# Revit family: Talos RDR-C03
name_source: partatom
category: Türen
revit_build: Autodesk Revit 2016 (Build: 20150220_1215(x64)
units: mm (PartAtom-declared; Revit-internal decimal feet)

## family parameters
Beim Laden mit Abzugskörper schneiden = Nein
Gemeinsam genutzt = Nein
Immer vertikal = Ja
OmniClass-Nummer = 23.30.10.00
OmniClass-Titel = Doors
Raumberechnungspunkt = Nein

## types (9) — shared parameters
Analytische Konstruktion = <Keine Auswahl>
BIMobject category = Revolving
CoverMaterial = Glas
Date of publishing = 1/16/2017
Design country = Germany
Edition number = 1
ElementWeight = 0.00 kg
FrameMaterial = 1.4401 - A4
Funktion = Außen
HandlePosition = 35 mm  [stored 0.114829 ft]
HasCover = Ja
HasFoldableDoors = Ja
HasGrabHandles = Ja
Hersteller = Kaba GmbH
Konstruktionstyp = Revolving Door
Manufacturer = Kaba GmbH
Manufacturer country = Germany
Manufacturer name = DORMA
Material main = Glass
Material secondary = Metal
Modell = Talos RDR-E01
MotorDriveType = -
Nominal height = 2300
OperatingWeight = 0.00 kg
Product Guid = dcba0ff2-2df2-4dff-90c3-13034e0ede75
Product SKU = Talos_RDR-C03
Product data url = https://bimobject.com
Product family = Entrance
Product group = Special Doors
ProfileWidth = 40 mm  [stored 0.131234 ft]
QR code = http://bimobject.com
RubberMaterial = Zellkautschuk - EPDM
SectionWidth = 4300 mm
ShutOffDevice = Nein
ShutOffDeviceInside = Nein
Technical description = http://www.kaba.com
Type = Talos RDR-C03
URL = http://www.kaba.com
Weight = 0.00 kg
zero-valued in all types: Nominal width, Weight Net (Kg)

## per-type parameters (varying)
- RDR-C03 2000: AccessLengthOrRadius=1030 mm; BaseType=60 mm - 169 mm; ClearHeight=2100 mm; ConsoleS1=1129 mm  [stored 3.70407 ft]; ConsoleS2=1129 mm  [stored 3.70407 ft]; ConsoleType=console : Type 4; CoverWidth=200 mm  [stored 0.656168 ft]; Diameter=1060 mm; DiameterCoverFront=1140 mm  [stored 3.74016 ft]; DiameterGlassInside=1040 mm  [stored 3.41207 ft]; DiameterGlassOutside=1050 mm  [stored 3.44488 ft]; DiameterNightLock=1090 mm  [stored 3.57612 ft]; DiameterNightLockCover=1120 mm; DiameterNightLockFrame=1081 mm  [stored 3.54659 ft]; DiameterNightLockGlassInside=1101 mm; DiameterNightLockGlassOutside=1109 mm  [stored 3.63845 ft]; Dicke=40 mm  [stored 0.131234 ft]; DoorThickness=40 mm  [stored 0.131234 ft]; DoorThicknessLeft=-20 mm  [stored -0.0656168 ft]; DoorThicknessRight=20 mm  [stored 0.0656168 ft]; DoorWidth=930 mm  [stored 3.05118 ft]; HandleMaterial=1.4401 - A4; HasConsoleS1=Ja; HasConsoleS2=Ja; HasGrabHandles 120=Nein; HasGrabHandles 180=Ja; HasIntegralShutOffDevice=Ja; HasLock=Ja; HasLockInside=Ja; HasMotionSensor=Ja; HasShellTopFrame=Nein; Height=2300 mm; MotionSensorInside=1122 mm  [stored 3.6811 ft]; MotionSensorOutside=1122 mm  [stored 3.6811 ft]; OuterDiameter=2100 mm; ProfileCenter=0 mm  [stored 0 ft]; RotationInterval 120=Nein; RotationInterval 180=Ja; StandardUsed=Talos RDR-C01-32; Width=2100 mm
- RDR-C03 2200: AccessLengthOrRadius=1130 mm; BaseType=60 mm - 69 mm; ClearHeight=2300 mm; ConsoleS1=1181 mm; ConsoleS2=1229 mm; ConsoleType=console : Type 5; CoverWidth=100 mm  [stored 0.328084 ft]; Diameter=1160 mm; DiameterCoverFront=1240 mm; DiameterGlassInside=1140 mm  [stored 3.74016 ft]; DiameterGlassOutside=1150 mm; DiameterNightLock=1190 mm  [stored 3.9042 ft]; DiameterNightLockCover=1220 mm  [stored 4.00262 ft]; DiameterNightLockFrame=1181 mm; DiameterNightLockGlassInside=1201 mm; DiameterNightLockGlassOutside=1209 mm  [stored 3.96654 ft]; Dicke=25 mm  [stored 0.082021 ft]; DoorThickness=25 mm  [stored 0.082021 ft]; DoorThicknessLeft=-12.5 mm; DoorThicknessRight=12.5 mm; DoorWidth=1030 mm; HandleMaterial=1.4401 - A4; HasConsoleS1=Ja; HasConsoleS2=Ja; HasGrabHandles 120=Ja; HasGrabHandles 180=Nein; HasIntegralShutOffDevice=Nein; HasLock=Ja; HasLockInside=Nein; HasMotionSensor=Ja; HasShellTopFrame=Nein; Height=2400 mm; MotionSensorInside=1160 mm; MotionSensorOutside=1222 mm; OuterDiameter=2300 mm; ProfileCenter=7.5 mm; RotationInterval 120=Ja; RotationInterval 180=Nein; StandardUsed=Talos RDR-C01-33; Width=2300 mm
- RDR-C03 2400: AccessLengthOrRadius=1230 mm  [stored 4.03543 ft]; BaseType=60 mm - 69 mm; ClearHeight=2300 mm; ConsoleS1=1281 mm; ConsoleS2=1281 mm; ConsoleType=console : Type 4; CoverWidth=300 mm; Diameter=1260 mm  [stored 4.13386 ft]; DiameterCoverFront=1340 mm; DiameterGlassInside=1240 mm; DiameterGlassOutside=1250 mm  [stored 4.10105 ft]; DiameterNightLock=1290 mm; DiameterNightLockCover=1320 mm; DiameterNightLockFrame=1281 mm; DiameterNightLockGlassInside=1301 mm; DiameterNightLockGlassOutside=1309 mm; Dicke=25 mm  [stored 0.082021 ft]; DoorThickness=25 mm  [stored 0.082021 ft]; DoorThicknessLeft=-12.5 mm; DoorThicknessRight=12.5 mm; DoorWidth=1130 mm; HandleMaterial=PA6.6 Gf30(schwarz); HasConsoleS1=Ja; HasConsoleS2=Ja; HasGrabHandles 120=Nein; HasGrabHandles 180=Ja; HasIntegralShutOffDevice=Nein; HasLock=Nein; HasLockInside=Nein; HasMotionSensor=Nein; HasShellTopFrame=Ja; Height=2600 mm; MotionSensorInside=1260 mm  [stored 4.13386 ft]; MotionSensorOutside=1260 mm  [stored 4.13386 ft]; OuterDiameter=2500 mm; ProfileCenter=7.5 mm; RotationInterval 120=Nein; RotationInterval 180=Ja; StandardUsed=Talos RDR-C01-34; Width=2500 mm
- RDR-C03 2600: AccessLengthOrRadius=1330 mm; BaseType=60 mm - 99 mm; ClearHeight=2100 mm; ConsoleS1=1381 mm; ConsoleS2=1381 mm; ConsoleType=console : Type 5; CoverWidth=200 mm  [stored 0.656168 ft]; Diameter=1360 mm; DiameterCoverFront=1440 mm; DiameterGlassInside=1340 mm; DiameterGlassOutside=1350 mm; DiameterNightLock=1390 mm; DiameterNightLockCover=1420 mm; DiameterNightLockFrame=1381 mm; DiameterNightLockGlassInside=1401 mm; DiameterNightLockGlassOutside=1409 mm; Dicke=40 mm  [stored 0.131234 ft]; DoorThickness=40 mm  [stored 0.131234 ft]; DoorThicknessLeft=-20 mm  [stored -0.0656168 ft]; DoorThicknessRight=20 mm  [stored 0.0656168 ft]; DoorWidth=1230 mm  [stored 4.03543 ft]; HandleMaterial=1.4401 - A4; HasConsoleS1=Ja; HasConsoleS2=Ja; HasGrabHandles 120=Ja; HasGrabHandles 180=Nein; HasIntegralShutOffDevice=Nein; HasLock=Nein; HasLockInside=Nein; HasMotionSensor=Nein; HasShellTopFrame=Nein; Height=2300 mm; MotionSensorInside=1360 mm; MotionSensorOutside=1360 mm; OuterDiameter=2700 mm; ProfileCenter=0 mm  [stored 0 ft]; RotationInterval 120=Ja; RotationInterval 180=Nein; StandardUsed=Talos RDR-C01-35; Width=2700 mm
- RDR-C03 2800: AccessLengthOrRadius=1430 mm; BaseType=60 mm - 190 mm; ClearHeight=2200 mm; ConsoleS1=1481 mm; ConsoleS2=1481 mm; ConsoleType=console : Type 4; CoverWidth=300 mm; Diameter=1460 mm; DiameterCoverFront=1540 mm; DiameterGlassInside=1440 mm; DiameterGlassOutside=1450 mm; DiameterNightLock=1490 mm; DiameterNightLockCover=1520 mm; DiameterNightLockFrame=1481 mm; DiameterNightLockGlassInside=1501 mm; DiameterNightLockGlassOutside=1509 mm; Dicke=40 mm  [stored 0.131234 ft]; DoorThickness=40 mm  [stored 0.131234 ft]; DoorThicknessLeft=-20 mm  [stored -0.0656168 ft]; DoorThicknessRight=20 mm  [stored 0.0656168 ft]; DoorWidth=1330 mm; HandleMaterial=PA6.6 Gf30(schwarz); HasConsoleS1=Nein; HasConsoleS2=Nein; HasGrabHandles 120=Nein; HasGrabHandles 180=Ja; HasIntegralShutOffDevice=Nein; HasLock=Nein; HasLockInside=Nein; HasMotionSensor=Nein; HasShellTopFrame=Ja; Height=2500 mm; MotionSensorInside=1460 mm; MotionSensorOutside=1460 mm; OuterDiameter=2900 mm; ProfileCenter=0 mm  [stored 0 ft]; RotationInterval 120=Nein; RotationInterval 180=Ja; StandardUsed=Talos RDR-C01-36; Width=2900 mm
- RDR-C03 3000: AccessLengthOrRadius=1530 mm; BaseType=60 mm - 129 mm; ClearHeight=2300 mm; ConsoleS1=1581 mm; ConsoleS2=1581 mm; ConsoleType=console : Type 5; CoverWidth=200 mm  [stored 0.656168 ft]; Diameter=1560 mm; DiameterCoverFront=1640 mm; DiameterGlassInside=1540 mm; DiameterGlassOutside=1550 mm; DiameterNightLock=1590 mm; DiameterNightLockCover=1620 mm; DiameterNightLockFrame=1581 mm; DiameterNightLockGlassInside=1601 mm; DiameterNightLockGlassOutside=1609 mm; Dicke=40 mm  [stored 0.131234 ft]; DoorThickness=40 mm  [stored 0.131234 ft]; DoorThicknessLeft=-20 mm  [stored -0.0656168 ft]; DoorThicknessRight=20 mm  [stored 0.0656168 ft]; DoorWidth=1430 mm; HandleMaterial=1.4401 - A4; HasConsoleS1=Nein; HasConsoleS2=Nein; HasGrabHandles 120=Ja; HasGrabHandles 180=Nein; HasIntegralShutOffDevice=Nein; HasLock=Nein; HasLockInside=Nein; HasMotionSensor=Nein; HasShellTopFrame=Nein; Height=2500 mm; MotionSensorInside=1560 mm; MotionSensorOutside=1560 mm; OuterDiameter=3100 mm; ProfileCenter=0 mm  [stored 0 ft]; RotationInterval 120=Ja; RotationInterval 180=Nein; StandardUsed=Talos RDR-C01-37; Width=3100 mm
- RDR-C03 3200: AccessLengthOrRadius=1630 mm; BaseType=60 mm - 149 mm; ClearHeight=2100 mm; ConsoleS1=1681 mm; ConsoleS2=1681 mm; ConsoleType=console : Type 4; CoverWidth=200 mm  [stored 0.656168 ft]; Diameter=1660 mm; DiameterCoverFront=1740 mm; DiameterGlassInside=1640 mm; DiameterGlassOutside=1650 mm; DiameterNightLock=1690 mm; DiameterNightLockCover=1720 mm; DiameterNightLockFrame=1681 mm; DiameterNightLockGlassInside=1701 mm; DiameterNightLockGlassOutside=1709 mm; Dicke=40 mm  [stored 0.131234 ft]; DoorThickness=40 mm  [stored 0.131234 ft]; DoorThicknessLeft=-20 mm  [stored -0.0656168 ft]; DoorThicknessRight=20 mm  [stored 0.0656168 ft]; DoorWidth=1530 mm; HandleMaterial=PA6.6 Gf30(schwarz); HasConsoleS1=Nein; HasConsoleS2=Nein; HasGrabHandles 120=Nein; HasGrabHandles 180=Ja; HasIntegralShutOffDevice=Nein; HasLock=Nein; HasLockInside=Nein; HasMotionSensor=Nein; HasShellTopFrame=Ja; Height=2300 mm; MotionSensorInside=1660 mm; MotionSensorOutside=1660 mm; OuterDiameter=3300 mm; ProfileCenter=0 mm  [stored 0 ft]; RotationInterval 120=Nein; RotationInterval 180=Ja; StandardUsed=Talos RDR-C01-38; Width=3300 mm
- RDR-C03 3400: AccessLengthOrRadius=1730 mm; BaseType=60 mm - 169 mm; ClearHeight=2100 mm; ConsoleS1=1829 mm; ConsoleS2=1829 mm; ConsoleType=console : Type 4; CoverWidth=200 mm  [stored 0.656168 ft]; Diameter=1760 mm; DiameterCoverFront=1840 mm; DiameterGlassInside=1740 mm; DiameterGlassOutside=1750 mm; DiameterNightLock=1790 mm; DiameterNightLockCover=1820 mm; DiameterNightLockFrame=1781 mm; DiameterNightLockGlassInside=1801 mm; DiameterNightLockGlassOutside=1809 mm; Dicke=40 mm  [stored 0.131234 ft]; DoorThickness=40 mm  [stored 0.131234 ft]; DoorThicknessLeft=-20 mm  [stored -0.0656168 ft]; DoorThicknessRight=20 mm  [stored 0.0656168 ft]; DoorWidth=1630 mm; HandleMaterial=1.4401 - A4; HasConsoleS1=Ja; HasConsoleS2=Ja; HasGrabHandles 120=Nein; HasGrabHandles 180=Ja; HasIntegralShutOffDevice=Ja; HasLock=Ja; HasLockInside=Ja; HasMotionSensor=Ja; HasShellTopFrame=Nein; Height=2300 mm; MotionSensorInside=1822 mm; MotionSensorOutside=1822 mm; OuterDiameter=3500 mm; ProfileCenter=0 mm  [stored 0 ft]; RotationInterval 120=Nein; RotationInterval 180=Ja; StandardUsed=Talos RDR-C01-39; Width=3500 mm
- RDR-C03 3600: AccessLengthOrRadius=1830 mm; BaseType=60 mm - 169 mm; ClearHeight=2100 mm; ConsoleS1=1929 mm; ConsoleS2=1929 mm; ConsoleType=console : Type 4; CoverWidth=200 mm  [stored 0.656168 ft]; Diameter=1860 mm; DiameterCoverFront=1940 mm; DiameterGlassInside=1840 mm; DiameterGlassOutside=1850 mm; DiameterNightLock=1890 mm; DiameterNightLockCover=1920 mm; DiameterNightLockFrame=1881 mm; DiameterNightLockGlassInside=1901 mm; DiameterNightLockGlassOutside=1909 mm; Dicke=40 mm  [stored 0.131234 ft]; DoorThickness=40 mm  [stored 0.131234 ft]; DoorThicknessLeft=-20 mm  [stored -0.0656168 ft]; DoorThicknessRight=20 mm  [stored 0.0656168 ft]; DoorWidth=1730 mm; HandleMaterial=1.4401 - A4; HasConsoleS1=Ja; HasConsoleS2=Nein; HasGrabHandles 120=Nein; HasGrabHandles 180=Ja; HasIntegralShutOffDevice=Ja; HasLock=Ja; HasLockInside=Ja; HasMotionSensor=Ja; HasShellTopFrame=Nein; Height=2300 mm; MotionSensorInside=1922 mm; MotionSensorOutside=1922 mm; OuterDiameter=3700 mm; ProfileCenter=0 mm  [stored 0 ft]; RotationInterval 120=Nein; RotationInterval 180=Ja; StandardUsed=-; Width=3700 mm

note: [stored X ft] marks values corroborated as IEEE doubles in the binary element streams (Revit-internal decimal feet)
